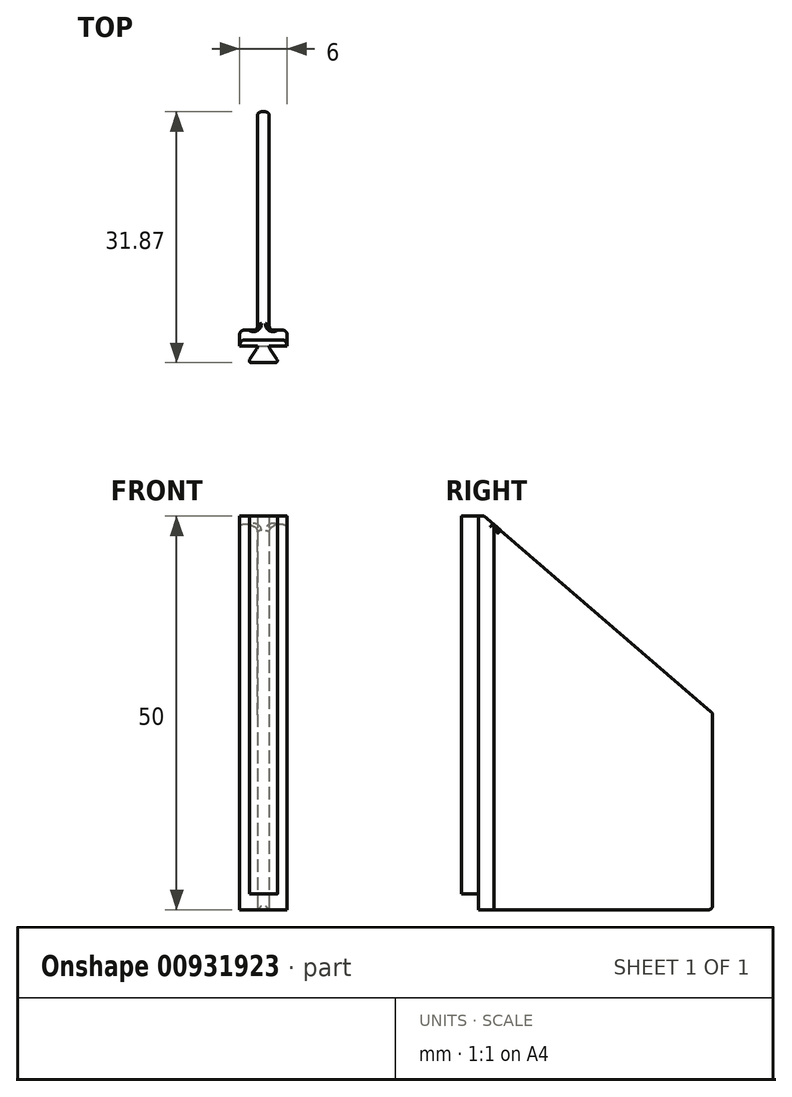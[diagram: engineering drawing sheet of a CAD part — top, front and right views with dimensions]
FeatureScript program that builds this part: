
annotation { "Feature Type Name" : "Feature", "Feature Type Description" : "" }
export const myFeature = defineFeature(function(context is Context, id is Id, definition is map)
    precondition{}
    {
        {
            assignVariable(context, id + "F0", {"name" : "FinHeight", "anyValue" : 50});
        }
        {
            assignVariable(context, id + "F1", {"name" : "FinLength", "anyValue" : 30});
        }
        {
            var Q0;
            Q0=qCreatedBy(makeId("Top.planeOp"),FACE);
            var sketch = newSketch(context, id + "F2", { "sketchPlane" : qUnion([Q0])});
            skLineSegment(sketch, "E0", {"start": v(-2, 0) * mm, "end": v(2, 0) * mm});
            skLineSegment(sketch, "E1", {"start": v(2, 0) * mm, "end": v(0.75, 1.87) * mm});
            skLineSegment(sketch, "E2", {"start": v(-2, 0) * mm, "end": v(-0.75, 1.87) * mm});
            skLineSegment(sketch, "E3", {"start": v(2, 0) * mm, "end": v(0, 0) * mm, "construction": true});
            skLineSegment(sketch, "E4", {"start": v(0, 0) * mm, "end": v(-2, 0) * mm, "construction": true});
            skLineSegment(sketch, "E5", {"start": v(-0.75, 1.87) * mm, "end": v(-0.75, 31.87) * mm});
            skLineSegment(sketch, "E6", {"start": v(-0.75, 31.87) * mm, "end": v(0.75, 31.87) * mm});
            skLineSegment(sketch, "E7", {"start": v(0.75, 31.87) * mm, "end": v(0.75, 1.87) * mm});
            skLineSegment(sketch, "E8", {"start": v(0, 6.57) * mm, "end": v(-0.75, 6.57) * mm, "construction": true});
            skLineSegment(sketch, "E9", {"start": v(0, 6.57) * mm, "end": v(0.75, 6.57) * mm, "construction": true});
            skLineSegment(sketch, "E10.bottom", {"start": v(-3, 4.12) * mm, "end": v(3, 4.12) * mm});
            skLineSegment(sketch, "E10.top", {"start": v(-3, 2.12) * mm, "end": v(3, 2.12) * mm});
            skLineSegment(sketch, "E10.left", {"start": v(-3, 4.12) * mm, "end": v(-3, 2.12) * mm});
            skLineSegment(sketch, "E10.right", {"start": v(3, 4.12) * mm, "end": v(3, 2.12) * mm});
            skPoint(sketch, "E10.middle", {"position": v(0, 3.12) * mm});
            skSolve(sketch);
        }
        {
            var Q0;
            {var subQ1=sQuery(id+"F2.wireOp",EDGE,"E5");var subQ3=sQuery(id+"F2.wireOp",EDGE,"E10.bottom");var subQ4=makeQuery(id+"F2.imprint","INTERSECT",VERTEX,{"derivedFrom":[subQ1,subQ3]});Q0=makeQuery(id+"F2.imprint","IMPRINT",FACE,{"disambiguationData":[TD([[makeQuery(id+"F2.imprint","IMPRINT",EDGE,{"disambiguationData":[TD([[subQ4,-1.0]])],"derivedFrom":subQ3}),-1.0]])]});}
            var Q1;
            {var subQ5=sQuery(id+"F2.wireOp",EDGE,"E10.right");Q1=makeQuery(id+"F2.imprint","IMPRINT",FACE,{"disambiguationData":[TD([[makeQuery(id+"F2.imprint","IMPRINT",EDGE,{"derivedFrom":subQ5}),-1.0]])]});}
            var Q2;
            {var subQ0=sQuery(id+"F2.wireOp",EDGE,"E6");Q2=makeQuery(id+"F2.imprint","IMPRINT",FACE,{"disambiguationData":[TD([[makeQuery(id+"F2.imprint","IMPRINT",EDGE,{"derivedFrom":subQ0}),-1.0]])]});}
            var Q3;
            {var subQ5=sQuery(id+"F2.wireOp",EDGE,"E10.left");Q3=makeQuery(id+"F2.imprint","IMPRINT",FACE,{"disambiguationData":[TD([[makeQuery(id+"F2.imprint","IMPRINT",EDGE,{"derivedFrom":subQ5}),1.0]])]});}
            extrude(context, id + "F3", {"entities" : qUnion([Q0, Q1, Q2, Q3]), "depth" : 50 * mm, "offsetDistance" : 25.4 * mm});
        }
        {
            var Q0;
            Q0=makeQuery(id+"F2.imprint","IMPRINT",FACE,{"disambiguationData":[TD([[makeQuery(id+"F2.imprint","IMPRINT",EDGE,{"derivedFrom":sQuery(id+"F2.wireOp",EDGE,"E0")}),1.0]])]});
            extrude(context, id + "F4", {"entities" : qUnion([Q0]), "operationType" : NewBodyOperationType.ADD, "depth" : (getVariable(context, 'FinHeight')) * mm, "offsetDistance" : 25 * mm, "hasSecondDirection" : true, "secondDirectionOppositeDirection" : false, "secondDirectionDepth" : 2 * mm});
        }
        {
            var Q0;
            Q0=makeQuery(id+"F3.opExtrude","CAP_EDGE",EDGE,{"disambiguationData":[OSD([sQuery(id+"F2.wireOp",EDGE,"E6")])],"isStart":false});
            chamfer(context, id + "F5", {"entities" : qUnion([Q0]), "chamferType" : ChamferType.TWO_OFFSETS, "width1" : (getVariable(context, 'FinHeight') / 2) * mm, "oppositeDirection" : false, "width2" : (getVariable(context, 'FinLength') - 1) * mm, "tangentPropagation" : true});
        }
        {
            var Q0;
            Q0=makeQuery(id+"F5.opChamfer","BLEND_EDGE",EDGE,{"blendedFrom":[makeQuery(id+"F3.opExtrude","CAP_EDGE",EDGE,{"disambiguationData":[OSD([sQuery(id+"F2.wireOp",EDGE,"E6")])],"isStart":false}),makeQuery(id+"F3.opExtrude","SWEPT_FACE",FACE,{"disambiguationData":[OSD([sQuery(id+"F2.wireOp",EDGE,"E7")])]})],"blendedInto":[makeQuery(id+"F3.opExtrude","SWEPT_FACE",FACE,{"disambiguationData":[OSD([sQuery(id+"F2.wireOp",EDGE,"E7")])]})]});
            var Q1;
            Q1=makeQuery(id+"F5.opChamfer","BLEND_EDGE",EDGE,{"blendedFrom":[makeQuery(id+"F3.opExtrude","CAP_EDGE",EDGE,{"disambiguationData":[OSD([sQuery(id+"F2.wireOp",EDGE,"E6")])],"isStart":false}),makeQuery(id+"F3.opExtrude","SWEPT_FACE",FACE,{"disambiguationData":[OSD([sQuery(id+"F2.wireOp",EDGE,"E5")])]})],"blendedInto":[makeQuery(id+"F3.opExtrude","SWEPT_FACE",FACE,{"disambiguationData":[OSD([sQuery(id+"F2.wireOp",EDGE,"E5")])]})]});
            var Q2;
            Q2=makeQuery(id+"F3.opExtrude","SWEPT_EDGE",EDGE,{"disambiguationData":[OSD([sQuery(id+"F2.wireOp",EDGE,"E6"),sQuery(id+"F2.wireOp",EDGE,"E7")])]});
            var Q3;
            Q3=makeQuery(id+"F3.opExtrude","SWEPT_EDGE",EDGE,{"disambiguationData":[OSD([sQuery(id+"F2.wireOp",EDGE,"E5"),sQuery(id+"F2.wireOp",EDGE,"E6")])]});
            var Q4;
            Q4=makeQuery(id+"F3.opExtrude","SWEPT_FACE",FACE,{"disambiguationData":[OSD([sQuery(id+"F2.wireOp",EDGE,"E6")])]});
            var Q5;
            Q5=makeQuery(id+"F3.opExtrude","SWEPT_EDGE",EDGE,{"disambiguationData":[OSD([sQuery(id+"F2.wireOp",EDGE,"E1"),sQuery(id+"F2.wireOp",EDGE,"E7")])]});
            var Q6;
            Q6=makeQuery(id+"F3.opExtrude","SWEPT_EDGE",EDGE,{"disambiguationData":[OSD([sQuery(id+"F2.wireOp",EDGE,"E2"),sQuery(id+"F2.wireOp",EDGE,"E5")])]});
            var Q7;
            Q7=makeQuery(id+"F3.opExtrude","SWEPT_EDGE",EDGE,{"disambiguationData":[OSD([sQuery(id+"F2.wireOp",EDGE,"E5"),sQuery(id+"F2.wireOp",EDGE,"E10.bottom")])]});
            var Q8;
            Q8=makeQuery(id+"F3.opExtrude","SWEPT_EDGE",EDGE,{"disambiguationData":[OSD([sQuery(id+"F2.wireOp",EDGE,"E7"),sQuery(id+"F2.wireOp",EDGE,"E10.bottom")])]});
            var Q9;
            Q9=makeQuery(id+"F3.opExtrude","SWEPT_EDGE",EDGE,{"disambiguationData":[OSD([sQuery(id+"F2.wireOp",EDGE,"E10.bottom"),sQuery(id+"F2.wireOp",EDGE,"E10.right")])]});
            var Q10;
            Q10=makeQuery(id+"F3.opExtrude","SWEPT_EDGE",EDGE,{"disambiguationData":[OSD([sQuery(id+"F2.wireOp",EDGE,"E10.bottom"),sQuery(id+"F2.wireOp",EDGE,"E10.left")])]});
            var Q11;
            Q11=makeQuery(id+"F5.opChamfer","BLEND_EDGE",EDGE,{"blendedFrom":[makeQuery(id+"F3.opExtrude","CAP_EDGE",EDGE,{"disambiguationData":[OSD([sQuery(id+"F2.wireOp",EDGE,"E6")])],"isStart":false}),makeQuery(id+"F3.opExtrude","SWEPT_FACE",FACE,{"disambiguationData":[OSD([sQuery(id+"F2.wireOp",EDGE,"E10.right")])]})],"blendedInto":[makeQuery(id+"F3.opExtrude","SWEPT_FACE",FACE,{"disambiguationData":[OSD([sQuery(id+"F2.wireOp",EDGE,"E10.right")])]})]});
            var Q12;
            Q12=makeQuery(id+"F5.opChamfer","BLEND_EDGE",EDGE,{"blendedFrom":[makeQuery(id+"F3.opExtrude","CAP_EDGE",EDGE,{"disambiguationData":[OSD([sQuery(id+"F2.wireOp",EDGE,"E6")])],"isStart":false}),makeQuery(id+"F3.opExtrude","SWEPT_FACE",FACE,{"disambiguationData":[OSD([sQuery(id+"F2.wireOp",EDGE,"E10.left")])]})],"blendedInto":[makeQuery(id+"F3.opExtrude","SWEPT_FACE",FACE,{"disambiguationData":[OSD([sQuery(id+"F2.wireOp",EDGE,"E10.left")])]})]});
            var Q13;
            Q13=makeQuery(id+"F4.opExtrude","SWEPT_EDGE",EDGE,{"disambiguationData":[OSD([sQuery(id+"F2.wireOp",EDGE,"E1"),sQuery(id+"F2.wireOp",EDGE,"E7"),sQuery(id+"F2.wireOp",EDGE,"E10.top")])]});
            var Q14;
            Q14=makeQuery(id+"F4.opExtrude","SWEPT_EDGE",EDGE,{"disambiguationData":[OSD([sQuery(id+"F2.wireOp",EDGE,"E2"),sQuery(id+"F2.wireOp",EDGE,"E5"),sQuery(id+"F2.wireOp",EDGE,"E10.top")])]});
            fillet(context, id + "F6", {"entities" : qUnion([Q0, Q1, Q2, Q3, Q4, Q5, Q6, Q7, Q8, Q9, Q10, Q11, Q12, Q13, Q14]), "radius" : .5 * mm, "tangentPropagation" : true, "allowEdgeOverflow" : false});
        }
        {
            var Q0;
            Q0=makeQuery(id+"F4.opExtrude","SWEPT_EDGE",EDGE,{"disambiguationData":[OSD([sQuery(id+"F2.wireOp",EDGE,"E0"),sQuery(id+"F2.wireOp",EDGE,"E1")])]});
            var Q1;
            Q1=makeQuery(id+"F4.opExtrude","SWEPT_EDGE",EDGE,{"disambiguationData":[OSD([sQuery(id+"F2.wireOp",EDGE,"E0"),sQuery(id+"F2.wireOp",EDGE,"E2")])]});
            fillet(context, id + "F7", {"entities" : qUnion([Q0, Q1]), "radius" : .25 * mm, "tangentPropagation" : true, "allowEdgeOverflow" : false});
        }
    });
